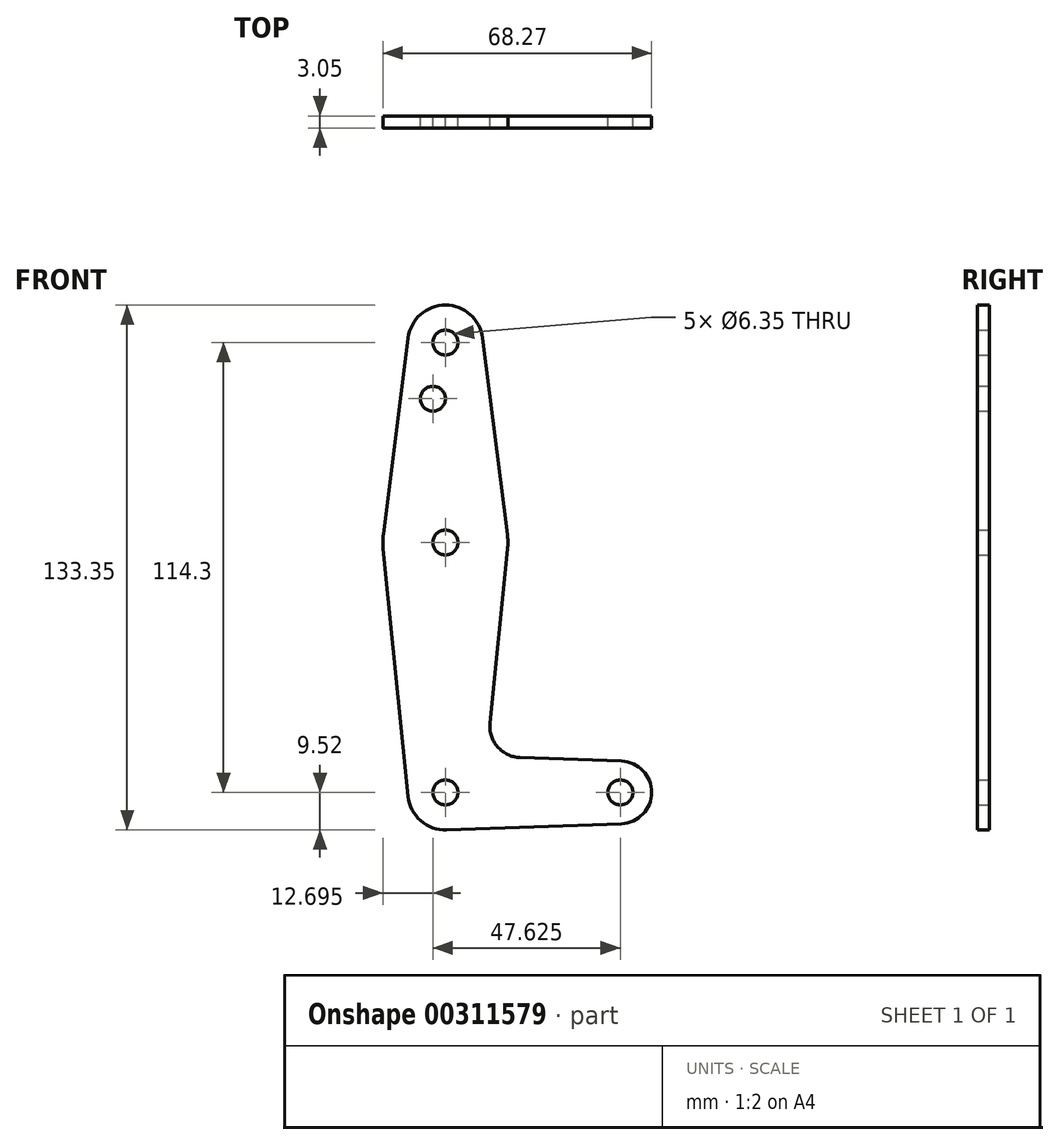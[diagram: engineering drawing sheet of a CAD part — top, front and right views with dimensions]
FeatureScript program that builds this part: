
annotation { "Feature Type Name" : "Feature", "Feature Type Description" : "" }
export const myFeature = defineFeature(function(context is Context, id is Id, definition is map)
    precondition{}
    {
        {
            var Q0;
            Q0=qCreatedBy(makeId("Front.planeOp"),FACE);
            var sketch = newSketch(context, id + "F0", { "sketchPlane" : qUnion([Q0])});
            skCircle(sketch, "E0", {"center": v(0, 0) * mm, "radius": 9.53 * mm});
            skLineSegment(sketch, "E1", {"start": v(0, 0) * mm, "end": v(0, 114.3) * mm});
            skLineSegment(sketch, "E2", {"start": v(0, 0) * mm, "end": v(44.45, 0) * mm});
            skCircle(sketch, "E3", {"center": v(0, 114.3) * mm, "radius": 9.53 * mm});
            skCircle(sketch, "E4", {"center": v(44.45, 0) * mm, "radius": 7.95 * mm});
            skCircle(sketch, "E5", {"center": v(0, 63.5) * mm, "radius": 15.88 * mm});
            skLineSegment(sketch, "E6", {"start": v(-15.75, 65.48) * mm, "end": v(-9.45, 115.5) * mm});
            skLineSegment(sketch, "E7", {"start": v(9.45, 115.5) * mm, "end": v(15.75, 65.48) * mm});
            skLineSegment(sketch, "E8", {"start": v(11.34, 17.6) * mm, "end": v(15.8, 61.91) * mm});
            skLineSegment(sketch, "E9", {"start": v(-9.48, -0.95) * mm, "end": v(-15.8, 61.91) * mm});
            skLineSegment(sketch, "E10", {"start": v(18.97, 8.86) * mm, "end": v(44.73, 7.95) * mm});
            skLineSegment(sketch, "E11", {"start": v(44.73, -7.95) * mm, "end": v(0.34, -9.52) * mm});
            skCircle(sketch, "E12", {"center": v(0, 63.5) * mm, "radius": 3.18 * mm});
            skCircle(sketch, "E13", {"center": v(0, 114.3) * mm, "radius": 3.18 * mm});
            skCircle(sketch, "E14", {"center": v(0, 0) * mm, "radius": 3.18 * mm});
            skCircle(sketch, "E15", {"center": v(44.45, 0) * mm, "radius": 3.18 * mm});
            skArc(sketch, "E16.filletArc", {"start": v(11.34, 17.6) * mm, "mid": v(13.26, 11.58) * mm, "end": v(18.97, 8.86) * mm});
            skCircle(sketch, "E17", {"center": v(-3.18, 100.03) * mm, "radius": 3.18 * mm});
            skSolve(sketch);
        }
        {
            var Q0;
            {var subQ0=sQuery(id+"F0.wireOp",EDGE,"E9");Q0=makeQuery(id+"F0.imprint","IMPRINT",FACE,{"disambiguationData":[TD([[makeQuery(id+"F0.imprint","IMPRINT",EDGE,{"derivedFrom":subQ0}),-1.0]])]});}
            var Q1;
            {var subQ5=sQuery(id+"F0.wireOp",EDGE,"E7");Q1=makeQuery(id+"F0.imprint","IMPRINT",FACE,{"disambiguationData":[TD([[makeQuery(id+"F0.imprint","IMPRINT",EDGE,{"derivedFrom":subQ5}),-1.0]])]});}
            var Q2;
            {var subQ0=sQuery(id+"F0.wireOp",EDGE,"E4");var subQ1=sQuery(id+"F0.wireOp",EDGE,"E2");var subQ2=makeQuery(id+"F0.imprint","INTERSECT",VERTEX,{"derivedFrom":[subQ1,subQ0]});Q2=makeQuery(id+"F0.imprint","IMPRINT",FACE,{"disambiguationData":[TD([[makeQuery(id+"F0.imprint","IMPRINT",EDGE,{"disambiguationData":[TD([[subQ2,1.0]])],"derivedFrom":subQ1}),1.0]])]});}
            var Q3;
            Q3=makeQuery(id+"F0.imprint","IMPRINT",FACE,{"disambiguationData":[TD([[makeQuery(id+"F0.imprint","IMPRINT",EDGE,{"derivedFrom":sQuery(id+"F0.wireOp",EDGE,"E13")}),-1.0]])]});
            var Q4;
            Q4=makeQuery(id+"F0.imprint","IMPRINT",FACE,{"disambiguationData":[TD([[makeQuery(id+"F0.imprint","IMPRINT",EDGE,{"derivedFrom":sQuery(id+"F0.wireOp",EDGE,"E15")}),-1.0]])]});
            var Q5;
            {var subQ0=sQuery(id+"F0.wireOp",EDGE,"E10");var subQ1=sQuery(id+"F0.wireOp",EDGE,"E0");var subQ2=makeQuery(id+"F0.imprint","INTERSECT",VERTEX,{"derivedFrom":[subQ1,subQ0]});Q5=makeQuery(id+"F0.imprint","IMPRINT",FACE,{"disambiguationData":[TD([[makeQuery(id+"F0.imprint","IMPRINT",EDGE,{"disambiguationData":[TD([[subQ2,1.0]])],"derivedFrom":subQ1}),-1.0]])]});}
            var Q6;
            {var subQ5=sQuery(id+"F0.wireOp",EDGE,"E0");var subQ7=sQuery(id+"F0.wireOp",EDGE,"E10");var subQ8=makeQuery(id+"F0.imprint","INTERSECT",VERTEX,{"derivedFrom":[subQ5,subQ7]});Q6=makeQuery(id+"F0.imprint","IMPRINT",FACE,{"disambiguationData":[TD([[makeQuery(id+"F0.imprint","IMPRINT",EDGE,{"disambiguationData":[TD([[subQ8,-1.0]])],"derivedFrom":subQ5}),-1.0]])]});}
            var Q7;
            {var subQ5=sQuery(id+"F0.wireOp",EDGE,"E11");Q7=makeQuery(id+"F0.imprint","IMPRINT",FACE,{"disambiguationData":[TD([[makeQuery(id+"F0.imprint","IMPRINT",EDGE,{"derivedFrom":subQ5}),-1.0]])]});}
            var Q8;
            {var subQ0=sQuery(id+"F0.wireOp",EDGE,"E5");var subQ2=sQuery(id+"F0.wireOp",EDGE,"E1");var subQ3=makeQuery(id+"F0.imprint","INTERSECT",VERTEX,{"disambiguationData":[OD(0.0)],"derivedFrom":[subQ2,subQ0]});Q8=makeQuery(id+"F0.imprint","IMPRINT",FACE,{"disambiguationData":[TD([[makeQuery(id+"F0.imprint","IMPRINT",EDGE,{"disambiguationData":[TD([[subQ3,-1.0]])],"derivedFrom":subQ2}),-1.0]])]});}
            var Q9;
            {var subQ0=sQuery(id+"F0.wireOp",EDGE,"E5");var subQ3=sQuery(id+"F0.wireOp",EDGE,"E1");var subQ8=makeQuery(id+"F0.imprint","INTERSECT",VERTEX,{"disambiguationData":[OD(0.0)],"derivedFrom":[subQ3,subQ0]});Q9=makeQuery(id+"F0.imprint","IMPRINT",FACE,{"disambiguationData":[TD([[makeQuery(id+"F0.imprint","IMPRINT",EDGE,{"disambiguationData":[TD([[subQ8,-1.0]])],"derivedFrom":subQ3}),1.0]])]});}
            var Q10;
            {var subQ0=sQuery(id+"F0.wireOp",EDGE,"E0");var subQ9=makeQuery(id+"F0.imprint","INTERSECT",VERTEX,{"derivedFrom":[subQ0,sQuery(id+"F0.wireOp",EDGE,"E9")]});Q10=makeQuery(id+"F0.imprint","IMPRINT",FACE,{"disambiguationData":[TD([[makeQuery(id+"F0.imprint","IMPRINT",EDGE,{"disambiguationData":[TD([[subQ9,1.0]])],"derivedFrom":subQ0}),1.0]])]});}
            var Q11;
            {var subQ1=sQuery(id+"F0.wireOp",EDGE,"E0");var subQ8=makeQuery(id+"F0.imprint","INTERSECT",VERTEX,{"derivedFrom":[subQ1,sQuery(id+"F0.wireOp",EDGE,"E10")]});Q11=makeQuery(id+"F0.imprint","IMPRINT",FACE,{"disambiguationData":[TD([[makeQuery(id+"F0.imprint","IMPRINT",EDGE,{"disambiguationData":[TD([[subQ8,1.0]])],"derivedFrom":subQ1}),1.0]])]});}
            var Q12;
            {var subQ5=sQuery(id+"F0.wireOp",EDGE,"E6");Q12=makeQuery(id+"F0.imprint","IMPRINT",FACE,{"disambiguationData":[TD([[makeQuery(id+"F0.imprint","IMPRINT",EDGE,{"derivedFrom":subQ5}),-1.0]])]});}
            var Q13;
            {var subQ0=sQuery(id+"F0.wireOp",EDGE,"E1");var subQ1=sQuery(id+"F0.wireOp",EDGE,"E0");var subQ2=makeQuery(id+"F0.imprint","INTERSECT",VERTEX,{"derivedFrom":[subQ1,subQ0]});Q13=makeQuery(id+"F0.imprint","IMPRINT",FACE,{"disambiguationData":[TD([[makeQuery(id+"F0.imprint","IMPRINT",EDGE,{"disambiguationData":[TD([[subQ2,1.0]])],"derivedFrom":subQ1}),1.0]])]});}
            extrude(context, id + "F1", {"entities" : qUnion([Q0, Q1, Q2, Q3, Q4, Q5, Q6, Q7, Q8, Q9, Q10, Q11, Q12, Q13]), "depth" : 3.05 * mm});
        }
    });
